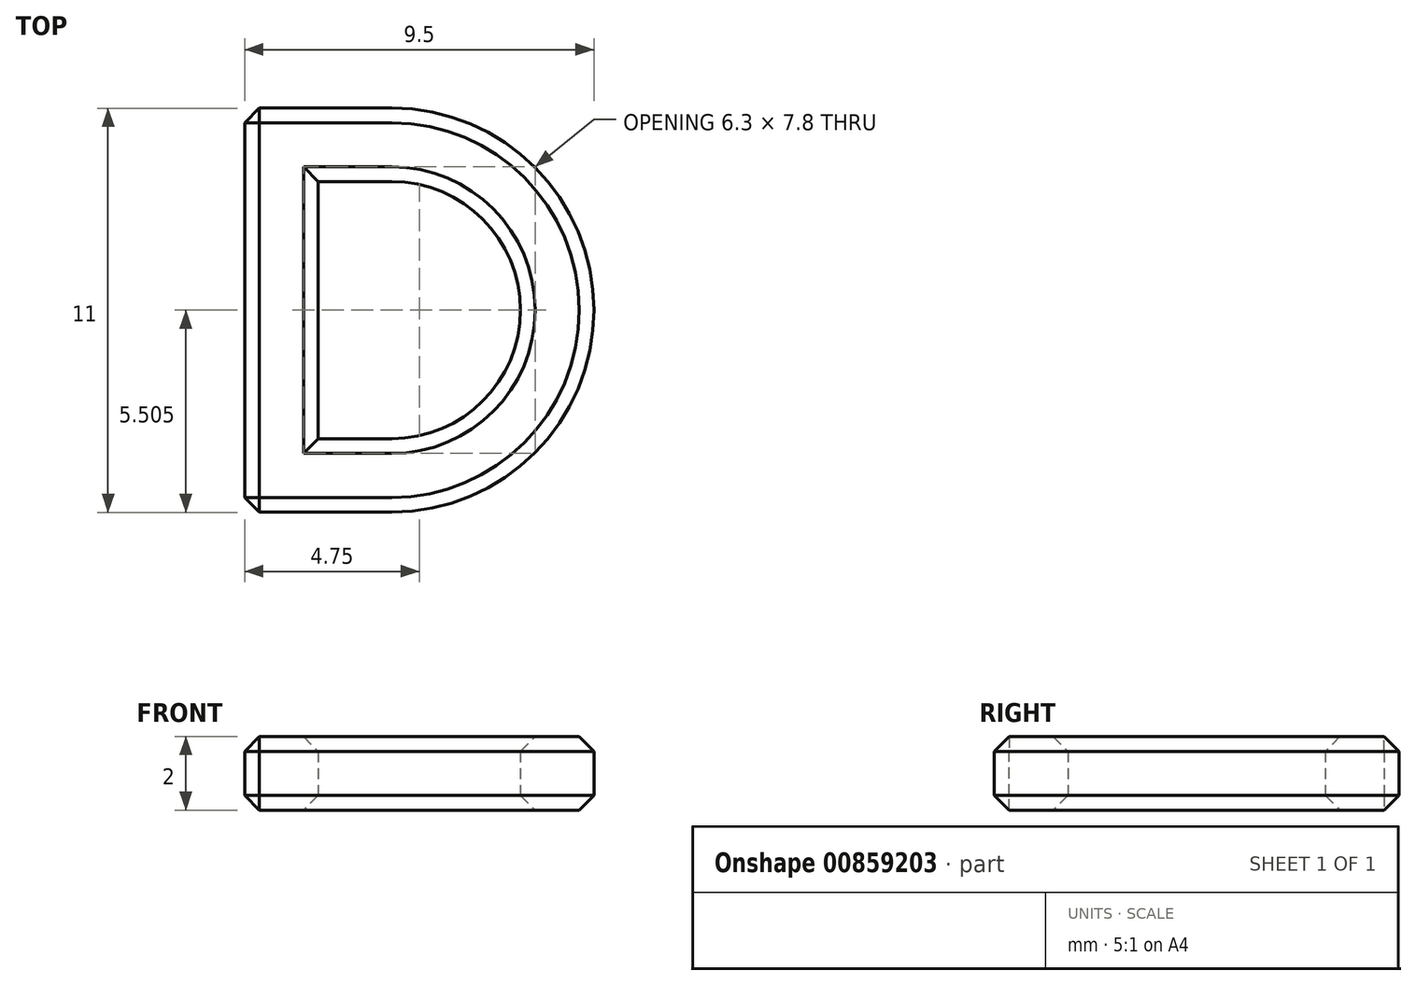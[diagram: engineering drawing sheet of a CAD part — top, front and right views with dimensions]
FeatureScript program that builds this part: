
annotation { "Feature Type Name" : "Feature", "Feature Type Description" : "" }
export const myFeature = defineFeature(function(context is Context, id is Id, definition is map)
    precondition{}
    {
        {
            var Q0;
            Q0=qCreatedBy(makeId("Top.planeOp"),FACE);
            var sketch = newSketch(context, id + "F0", { "sketchPlane" : qUnion([Q0])});
            skLineSegment(sketch, "E0.bottom", {"start": v(-12.33, -24.39) * mm, "end": v(-8.33, -24.39) * mm});
            skLineSegment(sketch, "E0.top", {"start": v(-12.33, -35.39) * mm, "end": v(-8.33, -35.39) * mm});
            skLineSegment(sketch, "E0.left", {"start": v(-12.33, -24.39) * mm, "end": v(-12.33, -35.39) * mm});
            skLineSegment(sketch, "E1.bottom", {"start": v(-10.33, -26.39) * mm, "end": v(-8.33, -26.39) * mm});
            skLineSegment(sketch, "E1.top", {"start": v(-10.33, -33.39) * mm, "end": v(-8.33, -33.39) * mm});
            skLineSegment(sketch, "E1.left", {"start": v(-10.33, -26.39) * mm, "end": v(-10.33, -33.39) * mm});
            skLineSegment(sketch, "E1.right", {"start": v(-8.33, -26.39) * mm, "end": v(-8.33, -33.39) * mm});
            skArc(sketch, "E2", {"start": v(-8.33, -33.39) * mm, "mid": v(-4.83, -29.89) * mm, "end": v(-8.33, -26.39) * mm});
            skArc(sketch, "E3.0", {"start": v(-8.33, -35.39) * mm, "mid": v(-2.83, -29.89) * mm, "end": v(-8.33, -24.39) * mm});
            skSolve(sketch);
        }
        {
            var Q0;
            Q0=qSketchRegion(id+"F0",true);
            extrude(context, id + "F1", {"entities" : qUnion([Q0]), "depth" : 2 * mm, "offsetDistance" : 25 * mm});
        }
        {
            var Q0;
            Q0=makeQuery(id+"F1.opExtrude","CAP_EDGE",EDGE,{"disambiguationData":[OSD([sQuery(id+"F0.wireOp",EDGE,"E1.right")])],"isStart":false});
            var Q1;
            Q1=makeQuery(id+"F1.opExtrude","CAP_EDGE",EDGE,{"disambiguationData":[OSD([sQuery(id+"F0.wireOp",EDGE,"E1.top")])],"isStart":false});
            var Q2;
            Q2=makeQuery(id+"F1.opExtrude","CAP_EDGE",EDGE,{"disambiguationData":[OSD([sQuery(id+"F0.wireOp",EDGE,"E1.left")])],"isStart":false});
            var Q3;
            Q3=makeQuery(id+"F1.opExtrude","CAP_EDGE",EDGE,{"disambiguationData":[OSD([sQuery(id+"F0.wireOp",EDGE,"E1.bottom")])],"isStart":false});
            var Q4;
            Q4=makeQuery(id+"F1.opExtrude","CAP_EDGE",EDGE,{"disambiguationData":[OSD([sQuery(id+"F0.wireOp",EDGE,"E0.top")])],"isStart":false});
            var Q5;
            Q5=makeQuery(id+"F1.opExtrude","CAP_EDGE",EDGE,{"disambiguationData":[OSD([sQuery(id+"F0.wireOp",EDGE,"E0.left")])],"isStart":false});
            var Q6;
            Q6=makeQuery(id+"F1.opExtrude","SWEPT_EDGE",EDGE,{"disambiguationData":[OSD([sQuery(id+"F0.wireOp",EDGE,"E0.top"),sQuery(id+"F0.wireOp",EDGE,"E0.left")])]});
            var Q7;
            Q7=makeQuery(id+"F1.opExtrude","SWEPT_EDGE",EDGE,{"disambiguationData":[OSD([sQuery(id+"F0.wireOp",EDGE,"E0.top"),sQuery(id+"F0.wireOp",EDGE,"E0.right")])]});
            var Q8;
            Q8=makeQuery(id+"F1.opExtrude","CAP_EDGE",EDGE,{"disambiguationData":[OSD([sQuery(id+"F0.wireOp",EDGE,"E0.right")])],"isStart":false});
            var Q9;
            Q9=makeQuery(id+"F1.opExtrude","CAP_EDGE",EDGE,{"disambiguationData":[OSD([sQuery(id+"F0.wireOp",EDGE,"E0.bottom")])],"isStart":false});
            var Q10;
            Q10=makeQuery(id+"F1.opExtrude","SWEPT_EDGE",EDGE,{"disambiguationData":[OSD([sQuery(id+"F0.wireOp",EDGE,"E0.bottom"),sQuery(id+"F0.wireOp",EDGE,"E0.right")])]});
            var Q11;
            Q11=makeQuery(id+"F1.opExtrude","SWEPT_EDGE",EDGE,{"disambiguationData":[OSD([sQuery(id+"F0.wireOp",EDGE,"E0.bottom"),sQuery(id+"F0.wireOp",EDGE,"E0.left")])]});
            var Q12;
            Q12=makeQuery(id+"F1.opExtrude","CAP_EDGE",EDGE,{"disambiguationData":[OSD([sQuery(id+"F0.wireOp",EDGE,"E0.left")])],"isStart":true});
            var Q13;
            Q13=makeQuery(id+"F1.opExtrude","CAP_EDGE",EDGE,{"disambiguationData":[OSD([sQuery(id+"F0.wireOp",EDGE,"E1.left")])],"isStart":true});
            var Q14;
            Q14=makeQuery(id+"F1.opExtrude","CAP_EDGE",EDGE,{"disambiguationData":[OSD([sQuery(id+"F0.wireOp",EDGE,"E1.bottom")])],"isStart":true});
            var Q15;
            Q15=makeQuery(id+"F1.opExtrude","CAP_EDGE",EDGE,{"disambiguationData":[OSD([sQuery(id+"F0.wireOp",EDGE,"E0.bottom")])],"isStart":true});
            var Q16;
            Q16=makeQuery(id+"F1.opExtrude","CAP_EDGE",EDGE,{"disambiguationData":[OSD([sQuery(id+"F0.wireOp",EDGE,"E0.right")])],"isStart":true});
            var Q17;
            Q17=makeQuery(id+"F1.opExtrude","CAP_EDGE",EDGE,{"disambiguationData":[OSD([sQuery(id+"F0.wireOp",EDGE,"E1.right")])],"isStart":true});
            var Q18;
            Q18=makeQuery(id+"F1.opExtrude","CAP_EDGE",EDGE,{"disambiguationData":[OSD([sQuery(id+"F0.wireOp",EDGE,"E1.top")])],"isStart":true});
            var Q19;
            Q19=makeQuery(id+"F1.opExtrude","CAP_EDGE",EDGE,{"disambiguationData":[OSD([sQuery(id+"F0.wireOp",EDGE,"E0.top")])],"isStart":true});
            chamfer(context, id + "F2", {"entities" : qUnion([Q0, Q1, Q2, Q3, Q4, Q5, Q6, Q7, Q8, Q9, Q10, Q11, Q12, Q13, Q14, Q15, Q16, Q17, Q18, Q19]), "width" : .4 * mm, "tangentPropagation" : true});
        }
    });
